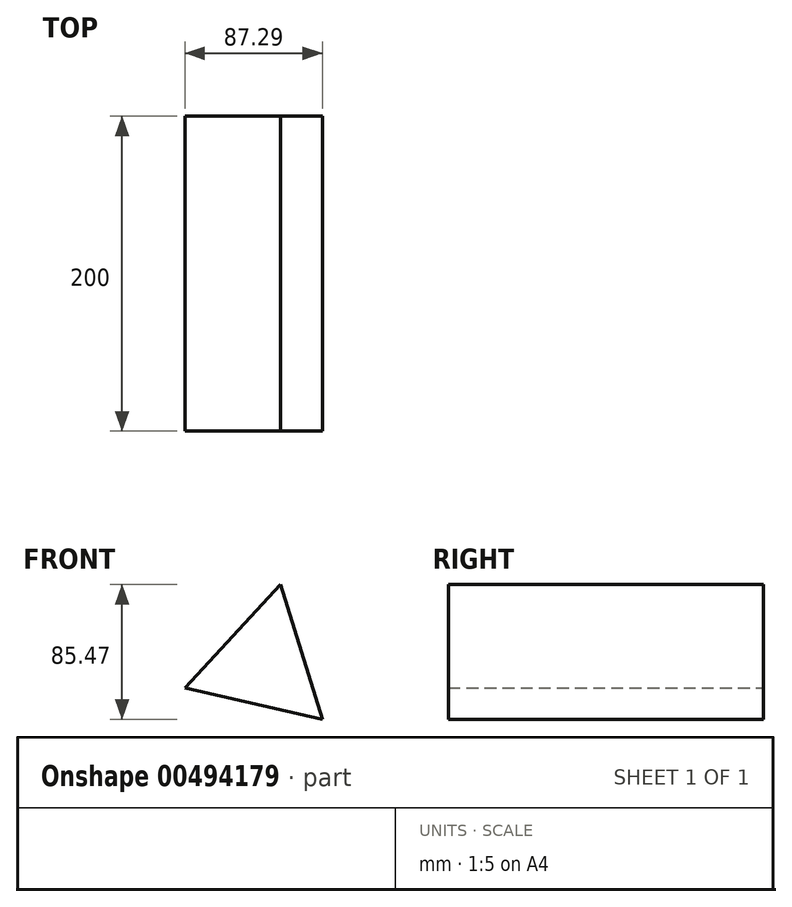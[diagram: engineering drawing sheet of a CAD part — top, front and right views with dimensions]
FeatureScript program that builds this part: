
annotation { "Feature Type Name" : "Feature", "Feature Type Description" : "" }
export const myFeature = defineFeature(function(context is Context, id is Id, definition is map)
    precondition{}
    {
        {
            var Q0;
            Q0=qCreatedBy(makeId("Front.planeOp"),FACE);
            var sketch = newSketch(context, id + "F0", { "sketchPlane" : qUnion([Q0])});
            skCircle(sketch, "E0.cCircle", {"center": v(0, 0) * mm, "radius": 51.67 * mm, "construction": true});
            skLineSegment(sketch, "E0.0", {"start": v(37.94, -35.08) * mm, "end": v(-49.35, -15.32) * mm});
            skLineSegment(sketch, "E0.1", {"start": v(-49.35, -15.32) * mm, "end": v(11.4, 50.4) * mm});
            skLineSegment(sketch, "E0.2", {"start": v(11.4, 50.4) * mm, "end": v(37.94, -35.08) * mm});
            skSolve(sketch);
        }
        {
            var Q0;
            Q0=makeQuery(id+"F0.imprint","IMPRINT",FACE,{"disambiguationData":[TD([[makeQuery(id+"F0.imprint","IMPRINT",EDGE,{"derivedFrom":sQuery(id+"F0.wireOp",EDGE,"E0.0")}),-1.0]])]});
            extrude(context, id + "F1", {"entities" : qUnion([Q0]), "depth" : 200 * mm});
        }
    });
